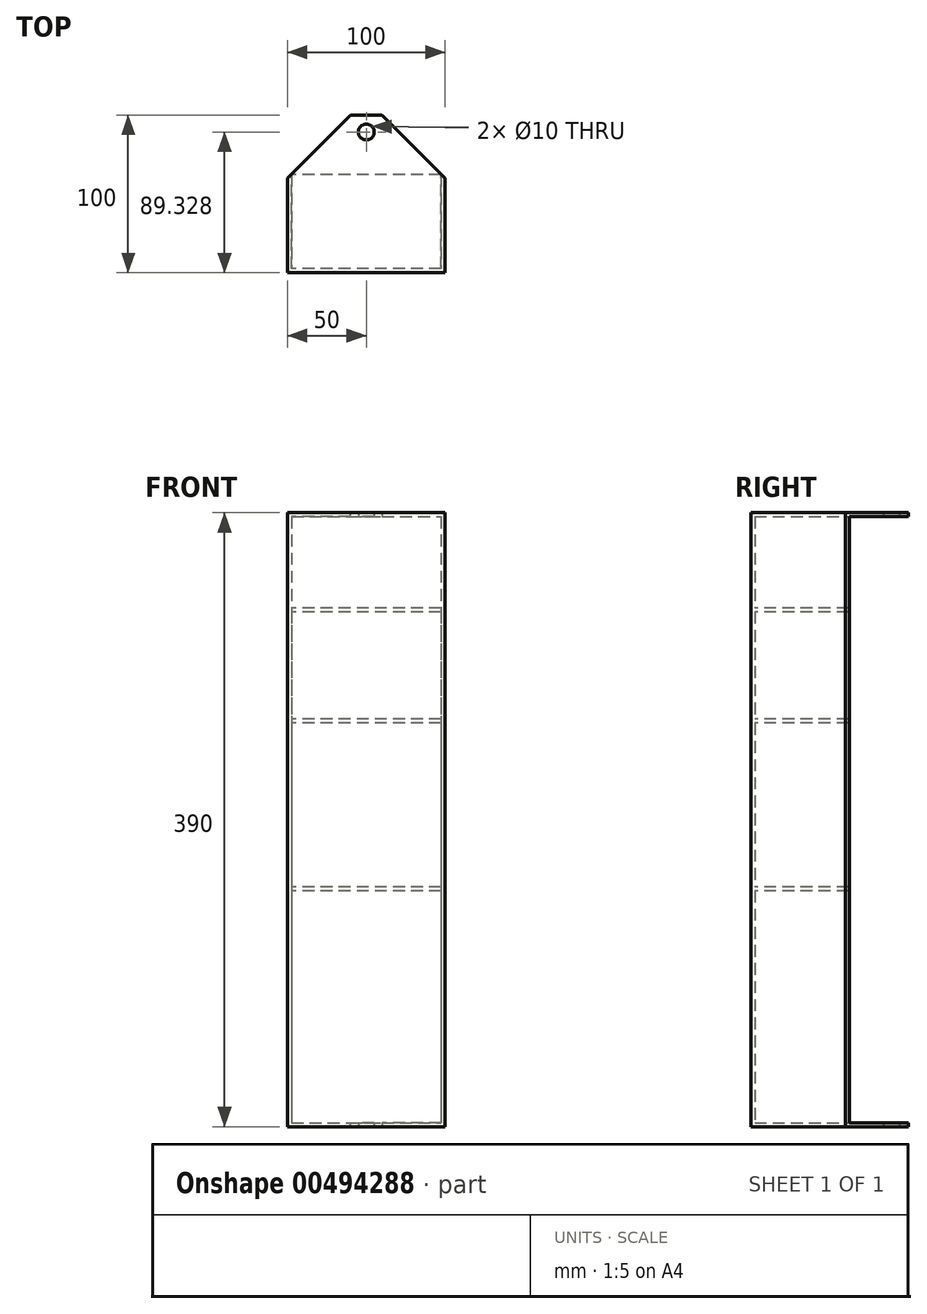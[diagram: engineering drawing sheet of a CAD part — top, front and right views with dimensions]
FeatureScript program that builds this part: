
annotation { "Feature Type Name" : "Feature", "Feature Type Description" : "" }
export const myFeature = defineFeature(function(context is Context, id is Id, definition is map)
    precondition{}
    {
        {
            var Q0;
            Q0=qCreatedBy(makeId("Top.planeOp"),FACE);
            var sketch = newSketch(context, id + "F0", { "sketchPlane" : qUnion([Q0])});
            skLineSegment(sketch, "E0.bottom", {"start": v(0, 0) * mm, "end": v(100, 0) * mm});
            skLineSegment(sketch, "E0.top", {"start": v(0, 100) * mm, "end": v(100, 100) * mm});
            skLineSegment(sketch, "E0.left", {"start": v(0, 0) * mm, "end": v(0, 100) * mm});
            skLineSegment(sketch, "E0.right", {"start": v(100, 0) * mm, "end": v(100, 100) * mm});
            skSolve(sketch);
        }
        {
            var Q0;
            Q0=makeQuery(id+"F0.imprint","IMPRINT",FACE,{"disambiguationData":[TD([[makeQuery(id+"F0.imprint","IMPRINT",EDGE,{"derivedFrom":sQuery(id+"F0.wireOp",EDGE,"E0.bottom")}),1.0]])]});
            extrude(context, id + "F1", {"entities" : qUnion([Q0]), "depth" : 390 * mm});
        }
        {
            var Q0;
            Q0=makeQuery(id+"F1.opExtrude","SWEPT_FACE",FACE,{"disambiguationData":[OSD([sQuery(id+"F0.wireOp",EDGE,"E0.top")])]});
            shell(context, id + "F2", {"entities" : qUnion([Q0]), "thickness" : 2.5 * mm});
        }
        {
            var Q0;
            Q0=makeQuery(id+"F1.opExtrude","CAP_FACE",FACE,{"disambiguationData":[OSD([sQuery(id+"F0.wireOp",EDGE,"E0.bottom"),sQuery(id+"F0.wireOp",EDGE,"E0.top"),sQuery(id+"F0.wireOp",EDGE,"E0.left"),sQuery(id+"F0.wireOp",EDGE,"E0.right")])],"isStart":true});
            var sketch = newSketch(context, id + "F3", { "sketchPlane" : qUnion([Q0])});
            skCircle(sketch, "E1", {"center": v(50, -89.33) * mm, "radius": 5 * mm});
            skPoint(sketch, "E1.centerSnap0", {"position": v(50, -100) * mm});
            skSolve(sketch);
        }
        {
            var Q0;
            Q0=makeQuery(id+"F3.imprint","IMPRINT",FACE,{"disambiguationData":[TD([[makeQuery(id+"F3.imprint","IMPRINT",EDGE,{"derivedFrom":sQuery(id+"F3.wireOp",EDGE,"E1")}),1.0]])]});
            extrude(context, id + "F4", {"entities" : qUnion([Q0]), "operationType" : NewBodyOperationType.REMOVE, "oppositeDirection" : true, "depth" : 2000 * mm});
        }
        {
            var Q0;
            Q0=makeQuery(id+"F1.opExtrude","SWEPT_EDGE",EDGE,{"disambiguationData":[OSD([sQuery(id+"F0.wireOp",EDGE,"E0.top"),sQuery(id+"F0.wireOp",EDGE,"E0.left")])]});
            var Q1;
            Q1=makeQuery(id+"F1.opExtrude","SWEPT_EDGE",EDGE,{"disambiguationData":[OSD([sQuery(id+"F0.wireOp",EDGE,"E0.top"),sQuery(id+"F0.wireOp",EDGE,"E0.right")])]});
            chamfer(context, id + "F5", {"entities" : qUnion([Q0, Q1]), "width" : 40 * mm, "tangentPropagation" : true});
        }
        {
            var Q0;
            Q0=makeQuery(id+"F2.opShell","OFFSET_FACE",FACE,{"disambiguationData":[OSD([sQuery(id+"F0.wireOp",EDGE,"E0.bottom")])]});
            var sketch = newSketch(context, id + "F6", { "sketchPlane" : qUnion([Q0])});
            skLineSegment(sketch, "E2.bottom", {"start": v(-97.5, 329.46) * mm, "end": v(-2.5, 329.46) * mm});
            skLineSegment(sketch, "E2.top", {"start": v(-97.5, 326.96) * mm, "end": v(-2.5, 326.96) * mm});
            skLineSegment(sketch, "E2.left", {"start": v(-97.5, 329.46) * mm, "end": v(-97.5, 326.96) * mm});
            skLineSegment(sketch, "E2.right", {"start": v(-2.5, 329.46) * mm, "end": v(-2.5, 326.96) * mm});
            skLineSegment(sketch, "E3.bottom", {"start": v(-97.5, 258.87) * mm, "end": v(-2.5, 258.87) * mm});
            skLineSegment(sketch, "E3.top", {"start": v(-97.5, 256.37) * mm, "end": v(-2.5, 256.37) * mm});
            skLineSegment(sketch, "E3.left", {"start": v(-97.5, 258.87) * mm, "end": v(-97.5, 256.37) * mm});
            skLineSegment(sketch, "E3.right", {"start": v(-2.5, 258.87) * mm, "end": v(-2.5, 256.37) * mm});
            skLineSegment(sketch, "E4.bottom", {"start": v(-97.5, 152.4) * mm, "end": v(-2.5, 152.4) * mm});
            skLineSegment(sketch, "E4.top", {"start": v(-97.5, 149.9) * mm, "end": v(-2.5, 149.9) * mm});
            skLineSegment(sketch, "E4.left", {"start": v(-97.5, 152.4) * mm, "end": v(-97.5, 149.9) * mm});
            skLineSegment(sketch, "E4.right", {"start": v(-2.5, 152.4) * mm, "end": v(-2.5, 149.9) * mm});
            skSolve(sketch);
        }
        {
            var Q0;
            Q0=makeQuery(id+"F6.imprint","IMPRINT",FACE,{"disambiguationData":[TD([[makeQuery(id+"F6.imprint","IMPRINT",EDGE,{"derivedFrom":sQuery(id+"F6.wireOp",EDGE,"E2.bottom")}),-1.0]])]});
            var Q1;
            Q1=makeQuery(id+"F6.imprint","IMPRINT",FACE,{"disambiguationData":[TD([[makeQuery(id+"F6.imprint","IMPRINT",EDGE,{"derivedFrom":sQuery(id+"F6.wireOp",EDGE,"E3.bottom")}),-1.0]])]});
            var Q2;
            Q2=makeQuery(id+"F6.imprint","IMPRINT",FACE,{"disambiguationData":[TD([[makeQuery(id+"F6.imprint","IMPRINT",EDGE,{"derivedFrom":sQuery(id+"F6.wireOp",EDGE,"E4.bottom")}),-1.0]])]});
            extrude(context, id + "F7", {"entities" : qUnion([Q0, Q1, Q2]), "operationType" : NewBodyOperationType.ADD, "depth" : 59.6 * mm});
        }
    });
